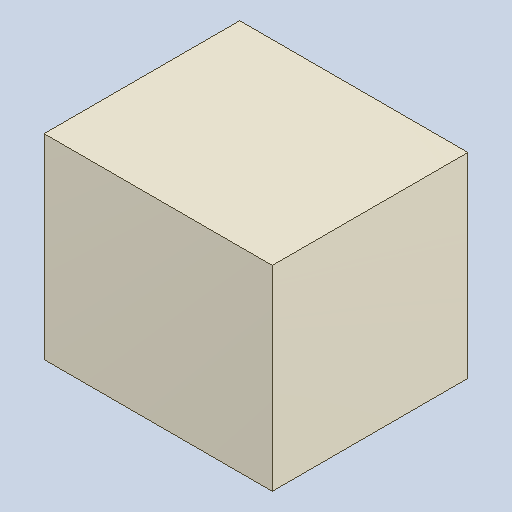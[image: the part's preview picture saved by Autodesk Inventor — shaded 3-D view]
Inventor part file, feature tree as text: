
AUTODESK INVENTOR PART (.ipt)
format: ipt  version: 2023.4 (Build 274418000, 418)  size: 82,432 bytes
history: native  units: mm
features: extrude x1
ambient origin geometry x8: Origin, YZ Plane, XZ Plane, XY Plane, X Axis, Y Axis, Z Axis, Center Point
bodies: Solid1 (feature_tree)
feature tree (1):
  extrude  "Extruded_7"  [1 undecoded]
note: 1 required parameter value undecoded (feature->parameter linkage not recoverable at this tier; creation-order binding heuristic only, values carry confidence <= 0.55)
